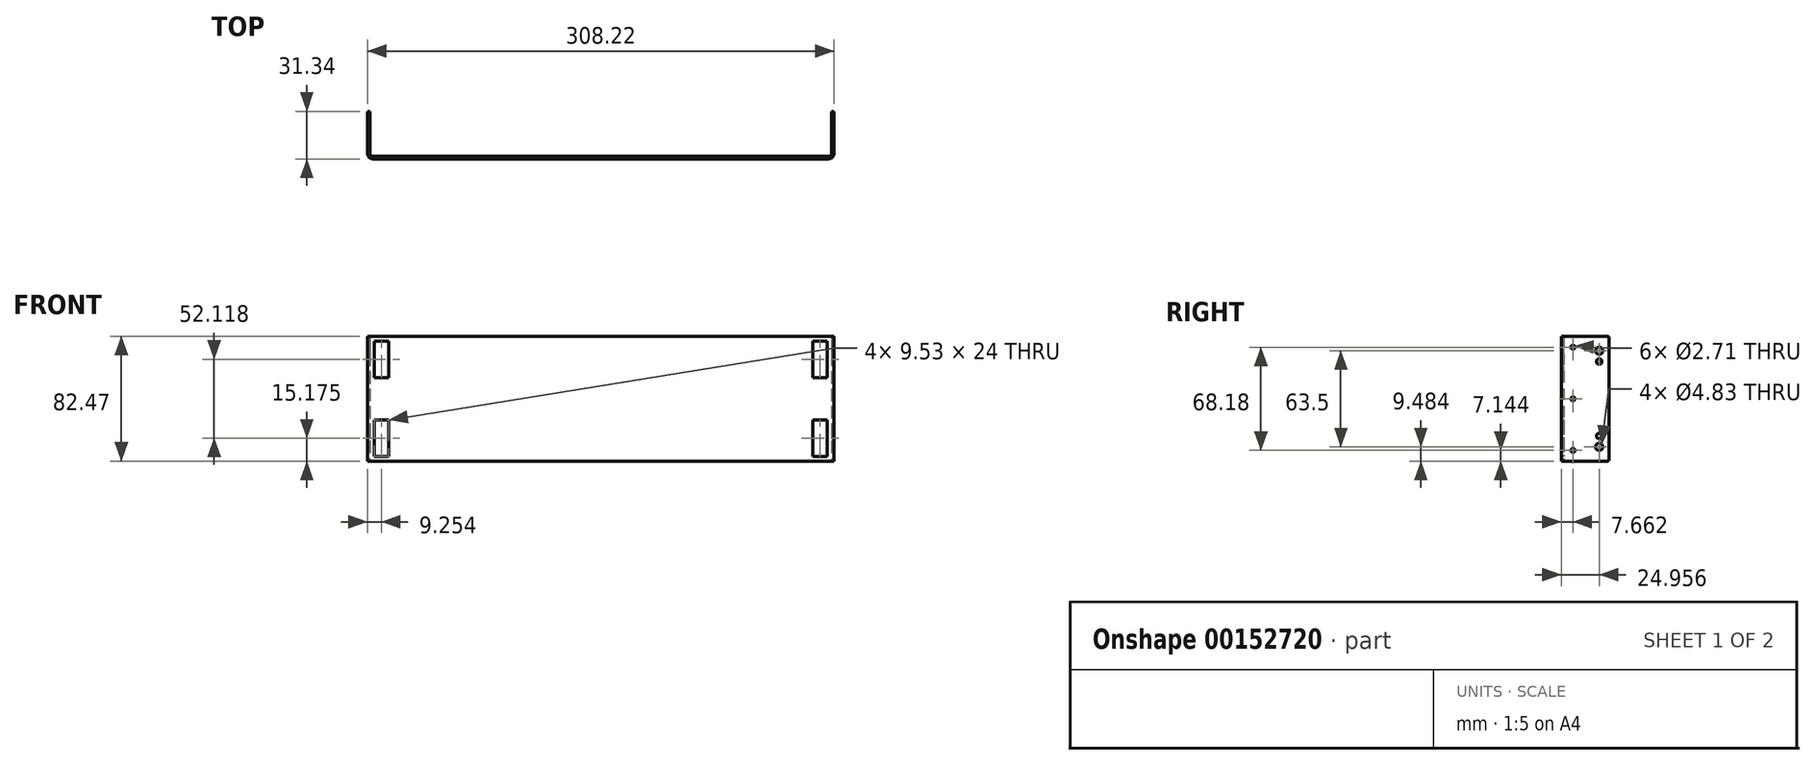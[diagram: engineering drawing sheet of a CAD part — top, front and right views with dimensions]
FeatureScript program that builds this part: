
annotation { "Feature Type Name" : "Feature", "Feature Type Description" : "" }
export const myFeature = defineFeature(function(context is Context, id is Id, definition is map)
    precondition{}
    {
        {
            var Q0;
            Q0=qCreatedBy(makeId("Top.planeOp"),FACE);
            var sketch = newSketch(context, id + "F0", { "sketchPlane" : qUnion([Q0])});
            skLineSegment(sketch, "E0.bottom", {"start": v(0, 0) * mm, "end": v(-304.8, 0) * mm});
            skLineSegment(sketch, "E0.top", {"start": v(1.7, -1.7) * mm, "end": v(-306.5, -1.7) * mm});
            skLineSegment(sketch, "E1.top", {"start": v(-304.8, 29.63) * mm, "end": v(-306.5, 29.63) * mm});
            skLineSegment(sketch, "E1.left", {"start": v(-304.8, 0) * mm, "end": v(-304.8, 29.63) * mm});
            skLineSegment(sketch, "E1.right", {"start": v(-306.5, -1.7) * mm, "end": v(-306.5, 29.63) * mm});
            skLineSegment(sketch, "E2.top", {"start": v(0, 29.63) * mm, "end": v(1.7, 29.63) * mm});
            skLineSegment(sketch, "E2.left", {"start": v(0, 0) * mm, "end": v(0, 29.63) * mm});
            skLineSegment(sketch, "E2.right", {"start": v(1.7, -1.7) * mm, "end": v(1.7, 29.63) * mm});
            skLineSegment(sketch, "E3", {"start": v(0, 0) * mm, "end": v(0, -1.7) * mm, "construction": true});
            skLineSegment(sketch, "E4", {"start": v(0, 0) * mm, "end": v(1.7, 0) * mm, "construction": true});
            skLineSegment(sketch, "E5", {"start": v(-304.8, 0) * mm, "end": v(-304.8, -1.7) * mm, "construction": true});
            skLineSegment(sketch, "E6", {"start": v(-304.8, 0) * mm, "end": v(-306.5, 0) * mm, "construction": true});
            skSolve(sketch);
        }
        {
            var Q0;
            Q0=qSketchRegion(id+"F0",true);
            extrude(context, id + "F1", {"entities" : qUnion([Q0]), "depth" : 82.47 * mm});
        }
        {
            var Q0;
            Q0=makeQuery(id+"F1.opExtrude","SWEPT_EDGE",EDGE,{"disambiguationData":[OSD([sQuery(id+"F0.wireOp",EDGE,"E0.bottom"),sQuery(id+"F0.wireOp",EDGE,"E2.left")])]});
            var Q1;
            Q1=makeQuery(id+"F1.opExtrude","SWEPT_EDGE",EDGE,{"disambiguationData":[OSD([sQuery(id+"F0.wireOp",EDGE,"E0.bottom"),sQuery(id+"F0.wireOp",EDGE,"E1.left")])]});
            fillet(context, id + "F2", {"entities" : qUnion([Q0, Q1]), "radius" : 1.98 * mm, "tangentPropagation" : true, "allowEdgeOverflow" : false});
        }
        {
            var Q0;
            Q0=makeQuery(id+"F1.opExtrude","SWEPT_EDGE",EDGE,{"disambiguationData":[OSD([sQuery(id+"F0.wireOp",EDGE,"E0.top"),sQuery(id+"F0.wireOp",EDGE,"E2.right")])]});
            var Q1;
            Q1=makeQuery(id+"F1.opExtrude","SWEPT_EDGE",EDGE,{"disambiguationData":[OSD([sQuery(id+"F0.wireOp",EDGE,"E0.top"),sQuery(id+"F0.wireOp",EDGE,"E1.right")])]});
            fillet(context, id + "F3", {"entities" : qUnion([Q0, Q1]), "radius" : 3.7 * mm, "tangentPropagation" : true, "allowEdgeOverflow" : false});
        }
        {
            var Q0;
            Q0=makeQuery(id+"F1.opExtrude","SWEPT_FACE",FACE,{"disambiguationData":[OSD([sQuery(id+"F0.wireOp",EDGE,"E1.right")])]});
            var sketch = newSketch(context, id + "F4", { "sketchPlane" : qUnion([Q0])});
            skLineSegment(sketch, "E7", {"start": v(-23.25, 0) * mm, "end": v(-23.25, 9.48) * mm, "construction": true});
            skLineSegment(sketch, "E8", {"start": v(-23.25, 72.98) * mm, "end": v(-23.25, 82.47) * mm, "construction": true});
            skLineSegment(sketch, "E9", {"start": v(-23.25, 41.23) * mm, "end": v(-29.63, 41.23) * mm, "construction": true});
            skCircle(sketch, "E10", {"center": v(-23.25, 9.48) * mm, "radius": 2.41 * mm});
            skCircle(sketch, "E11", {"center": v(-23.25, 72.98) * mm, "radius": 2.41 * mm});
            skLineSegment(sketch, "E12", {"start": v(-23.25, 9.48) * mm, "end": v(-23.25, 16.66) * mm, "construction": true});
            skLineSegment(sketch, "E13", {"start": v(-23.25, 16.66) * mm, "end": v(-23.25, 65.8) * mm, "construction": true});
            skLineSegment(sketch, "E14", {"start": v(-23.25, 65.8) * mm, "end": v(-23.25, 72.98) * mm, "construction": true});
            skCircle(sketch, "E15", {"center": v(-23.25, 65.8) * mm, "radius": 1.83 * mm});
            skCircle(sketch, "E16", {"center": v(-23.25, 16.66) * mm, "radius": 1.83 * mm});
            skLineSegment(sketch, "E17", {"start": v(-23.25, 41.23) * mm, "end": v(-5.95, 41.23) * mm, "construction": true});
            skLineSegment(sketch, "E18", {"start": v(-5.95, 7.14) * mm, "end": v(-5.95, 75.32) * mm, "construction": true});
            skLineSegment(sketch, "E19", {"start": v(-5.95, 41.23) * mm, "end": v(-1.98, 41.23) * mm, "construction": true});
            skLineSegment(sketch, "E20", {"start": v(-5.95, 7.14) * mm, "end": v(-5.95, 3.18) * mm, "construction": true});
            skLineSegment(sketch, "E21", {"start": v(-5.95, 75.32) * mm, "end": v(-5.95, 82.47) * mm, "construction": true});
            skCircle(sketch, "E22", {"center": v(-5.95, 7.14) * mm, "radius": 1.35 * mm});
            skCircle(sketch, "E23", {"center": v(-5.95, 75.32) * mm, "radius": 1.35 * mm});
            skCircle(sketch, "E24", {"center": v(-5.95, 41.23) * mm, "radius": 1.35 * mm});
            skSolve(sketch);
        }
        {
            var Q0;
            Q0 = qSketchRegion(id + "F4", true);
            var Q1;
            Q1=makeQuery(id+"F1.opExtrude","SWEPT_FACE",FACE,{"disambiguationData":[OSD([sQuery(id+"F0.wireOp",EDGE,"E2.right")])]});
            extrude(context, id + "F5", {"entities" : qUnion([Q0]), "operationType" : NewBodyOperationType.REMOVE, "endBound" : BoundingType.UP_TO_SURFACE, "oppositeDirection" : true, "endBoundEntityFace" : qUnion([Q1]), "depth" : 25.4 * mm});
        }
        {
            var Q0;
            Q0=makeQuery(id+"F1.opExtrude","SWEPT_FACE",FACE,{"disambiguationData":[OSD([sQuery(id+"F0.wireOp",EDGE,"E0.top")])]});
            var sketch = newSketch(context, id + "F6", { "sketchPlane" : qUnion([Q0])});
            skLineSegment(sketch, "E25", {"start": v(-1.98, 41.23) * mm, "end": v(-2.78, 41.23) * mm, "construction": true});
            skLineSegment(sketch, "E26", {"start": v(-2.78, 27.17) * mm, "end": v(-2.78, 55.3) * mm, "construction": true});
            skLineSegment(sketch, "E27", {"start": v(-302.82, 41.23) * mm, "end": v(-302.02, 41.23) * mm, "construction": true});
            skLineSegment(sketch, "E28", {"start": v(-302.02, 27.17) * mm, "end": v(-302.02, 55.3) * mm, "construction": true});
            skLineSegment(sketch, "E29.bottom", {"start": v(-2.78, 27.17) * mm, "end": v(-12.31, 27.17) * mm});
            skLineSegment(sketch, "E29.top", {"start": v(-2.78, 3.18) * mm, "end": v(-12.31, 3.17) * mm});
            skLineSegment(sketch, "E29.left", {"start": v(-2.78, 27.17) * mm, "end": v(-2.78, 3.18) * mm});
            skLineSegment(sketch, "E29.right", {"start": v(-12.31, 27.17) * mm, "end": v(-12.31, 3.17) * mm});
            skLineSegment(sketch, "E30", {"start": v(-2.78, 3.18) * mm, "end": v(-2.78, 0) * mm, "construction": true});
            skLineSegment(sketch, "E31.bottom", {"start": v(-2.78, 55.3) * mm, "end": v(-12.31, 55.3) * mm});
            skLineSegment(sketch, "E31.top", {"start": v(-2.78, 79.3) * mm, "end": v(-12.31, 79.3) * mm});
            skLineSegment(sketch, "E31.left", {"start": v(-2.78, 55.3) * mm, "end": v(-2.78, 79.3) * mm});
            skLineSegment(sketch, "E31.right", {"start": v(-12.31, 55.3) * mm, "end": v(-12.31, 79.3) * mm});
            skLineSegment(sketch, "E32.bottom", {"start": v(-302.02, 55.3) * mm, "end": v(-292.49, 55.3) * mm});
            skLineSegment(sketch, "E32.top", {"start": v(-302.02, 79.3) * mm, "end": v(-292.49, 79.3) * mm});
            skLineSegment(sketch, "E32.left", {"start": v(-302.02, 55.3) * mm, "end": v(-302.02, 79.3) * mm});
            skLineSegment(sketch, "E32.right", {"start": v(-292.49, 55.3) * mm, "end": v(-292.49, 79.3) * mm});
            skLineSegment(sketch, "E33.bottom", {"start": v(-302.02, 27.17) * mm, "end": v(-292.49, 27.17) * mm});
            skLineSegment(sketch, "E33.top", {"start": v(-302.02, 3.17) * mm, "end": v(-292.49, 3.17) * mm});
            skLineSegment(sketch, "E33.left", {"start": v(-302.02, 27.17) * mm, "end": v(-302.02, 3.17) * mm});
            skLineSegment(sketch, "E33.right", {"start": v(-292.49, 27.17) * mm, "end": v(-292.49, 3.17) * mm});
            skSolve(sketch);
        }
        {
            var Q0;
            Q0 = qSketchRegion(id + "F6", true);
            var Q1;
            Q1=makeQuery(id+"F1.opExtrude","SWEPT_FACE",FACE,{"disambiguationData":[OSD([sQuery(id+"F0.wireOp",EDGE,"E1.top")])]});
            extrude(context, id + "F7", {"entities" : qUnion([Q0]), "operationType" : NewBodyOperationType.REMOVE, "endBound" : BoundingType.UP_TO_SURFACE, "oppositeDirection" : true, "endBoundEntityFace" : qUnion([Q1]), "depth" : 25.4 * mm});
        }
        {
            var Q0;
            Q0=makeQuery(id+"F1.opExtrude","CAP_EDGE",EDGE,{"disambiguationData":[OSD([sQuery(id+"F0.wireOp",EDGE,"E2.top")])],"isStart":false});
            var Q1;
            Q1=makeQuery(id+"F1.opExtrude","CAP_EDGE",EDGE,{"disambiguationData":[OSD([sQuery(id+"F0.wireOp",EDGE,"E2.top")])],"isStart":true});
            var Q2;
            Q2=makeQuery(id+"F1.opExtrude","CAP_EDGE",EDGE,{"disambiguationData":[OSD([sQuery(id+"F0.wireOp",EDGE,"E1.top")])],"isStart":true});
            var Q3;
            Q3=makeQuery(id+"F1.opExtrude","CAP_EDGE",EDGE,{"disambiguationData":[OSD([sQuery(id+"F0.wireOp",EDGE,"E1.top")])],"isStart":false});
            fillet(context, id + "F8", {"entities" : qUnion([Q0, Q1, Q2, Q3]), "radius" : 0.76 * mm, "tangentPropagation" : true, "allowEdgeOverflow" : false});
        }
    });
